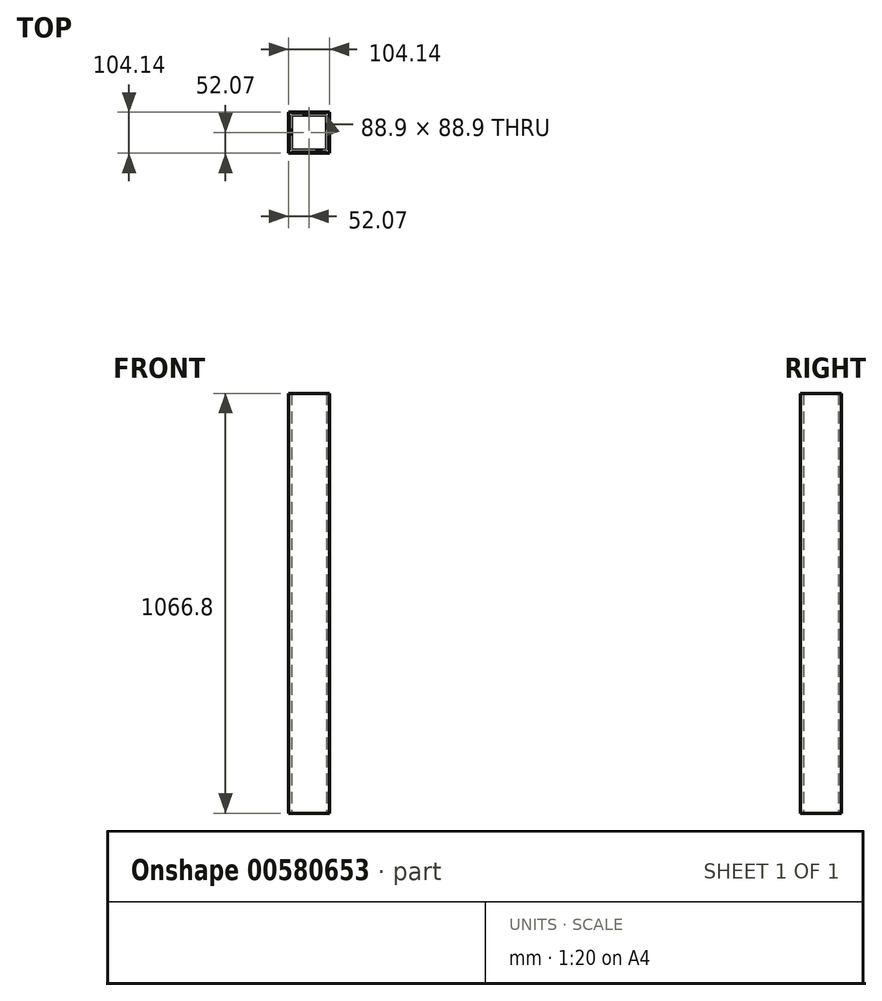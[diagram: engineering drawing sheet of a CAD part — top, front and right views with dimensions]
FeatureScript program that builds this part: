
annotation { "Feature Type Name" : "Feature", "Feature Type Description" : "" }
export const myFeature = defineFeature(function(context is Context, id is Id, definition is map)
    precondition{}
    {
        {
            var Q0;
            Q0=qCreatedBy(makeId("Top.planeOp"),FACE);
            var sketch = newSketch(context, id + "F0", { "sketchPlane" : qUnion([Q0])});
            skLineSegment(sketch, "E0.bottom", {"start": v(52.07, -52.07) * mm, "end": v(-52.07, -52.07) * mm});
            skLineSegment(sketch, "E0.top", {"start": v(52.07, 52.07) * mm, "end": v(-52.07, 52.07) * mm});
            skLineSegment(sketch, "E0.left", {"start": v(52.07, -52.07) * mm, "end": v(52.07, 52.07) * mm});
            skLineSegment(sketch, "E0.right", {"start": v(-52.07, -52.07) * mm, "end": v(-52.07, 52.07) * mm});
            skPoint(sketch, "E0.middle", {"position": v(0, 0) * mm});
            skLineSegment(sketch, "E1.bottom", {"start": v(44.45, -44.45) * mm, "end": v(-44.45, -44.45) * mm});
            skLineSegment(sketch, "E1.top", {"start": v(44.45, 44.45) * mm, "end": v(-44.45, 44.45) * mm});
            skLineSegment(sketch, "E1.left", {"start": v(44.45, -44.45) * mm, "end": v(44.45, 44.45) * mm});
            skLineSegment(sketch, "E1.right", {"start": v(-44.45, -44.45) * mm, "end": v(-44.45, 44.45) * mm});
            skSolve(sketch);
        }
        {
            var Q0;
            Q0=makeQuery(id+"F0.imprint","IMPRINT",FACE,{"disambiguationData":[TD([[makeQuery(id+"F0.imprint","IMPRINT",EDGE,{"derivedFrom":sQuery(id+"F0.wireOp",EDGE,"E0.bottom")}),-1.0]])]});
            extrude(context, id + "F1", {"entities" : qUnion([Q0]), "depth" : 1066.8 * mm, "offsetDistance" : 25.4 * mm});
        }
    });
